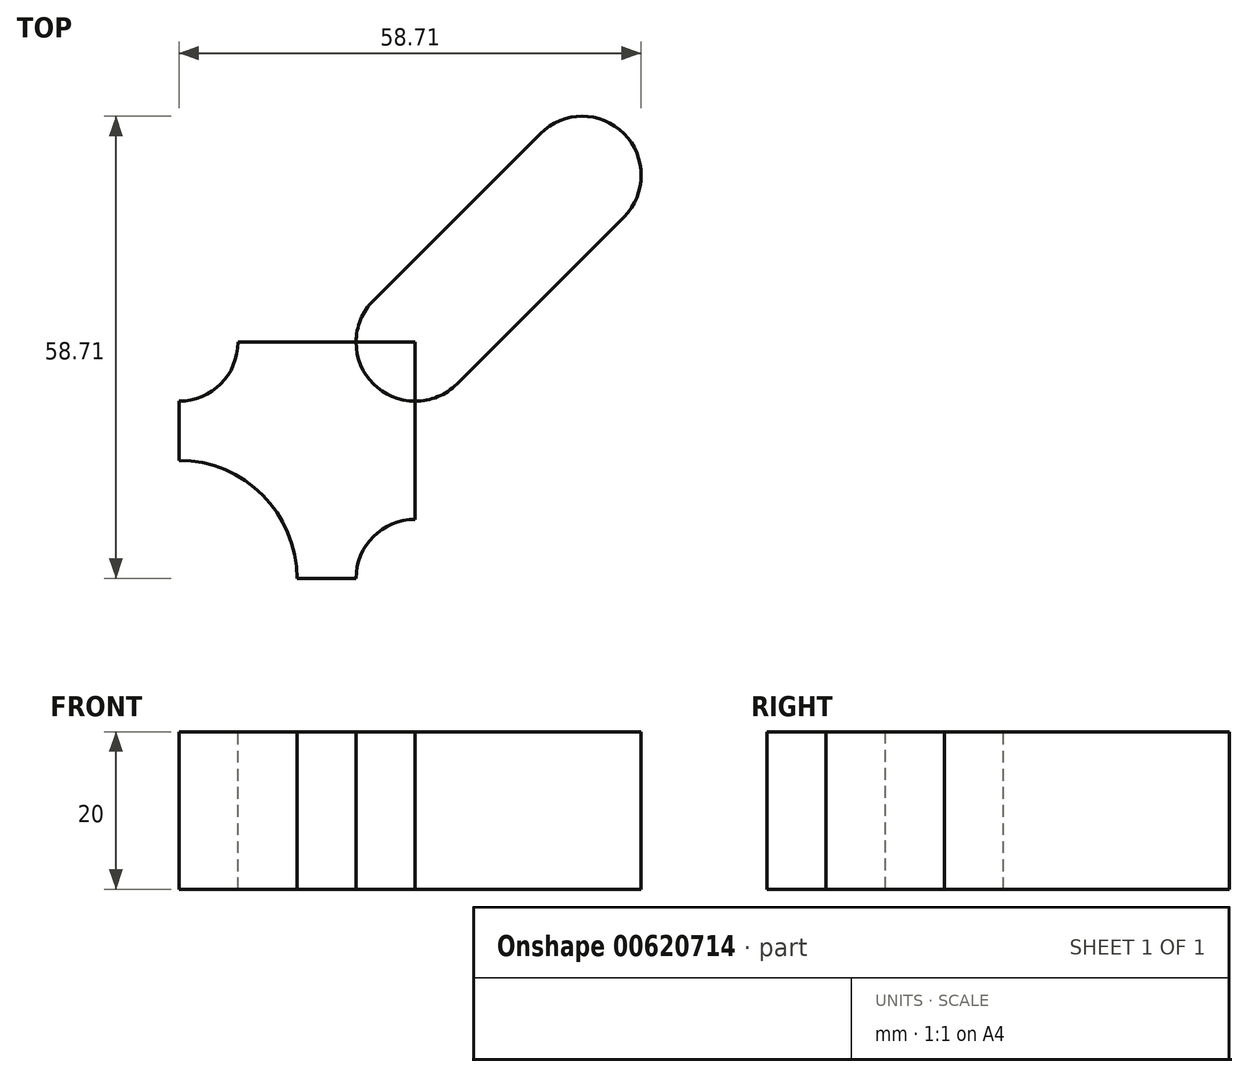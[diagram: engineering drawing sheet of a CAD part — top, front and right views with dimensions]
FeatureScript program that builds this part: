
annotation { "Feature Type Name" : "Feature", "Feature Type Description" : "" }
export const myFeature = defineFeature(function(context is Context, id is Id, definition is map)
    precondition{}
    {
        {
            var Q0;
            Q0=qCreatedBy(makeId("Top.planeOp"),FACE);
            var sketch = newSketch(context, id + "F0", { "sketchPlane" : qUnion([Q0])});
            skLineSegment(sketch, "E0.bottom", {"start": v(0, 0) * mm, "end": v(-45, 0) * mm});
            skLineSegment(sketch, "E0.left", {"start": v(0, 0) * mm, "end": v(0, 115) * mm});
            skArc(sketch, "E1", {"start": v(-45, 0) * mm, "mid": v(-55.6, 4.4) * mm, "end": v(-60, 15) * mm});
            skArc(sketch, "E2", {"start": v(-60, 15) * mm, "mid": v(-64.4, 25.6) * mm, "end": v(-75, 30) * mm});
            skArc(sketch, "E3", {"start": v(-75, 30) * mm, "mid": v(-85.6, 34.4) * mm, "end": v(-90, 45) * mm});
            skLineSegment(sketch, "E4", {"start": v(-45, 15) * mm, "end": v(-60, 15) * mm});
            skLineSegment(sketch, "E5", {"start": v(-60, 15) * mm, "end": v(-75, 15) * mm});
            skLineSegment(sketch, "E6", {"start": v(-75, 15) * mm, "end": v(-75, 30) * mm});
            skLineSegment(sketch, "E7", {"start": v(-75, 45) * mm, "end": v(-75, 30) * mm});
            skLineSegment(sketch, "E8", {"start": v(-75, 45) * mm, "end": v(-90, 45) * mm});
            skLineSegment(sketch, "E9", {"start": v(-90, 45) * mm, "end": v(-90, 65) * mm});
            skLineSegment(sketch, "E10", {"start": v(-95, 70) * mm, "end": v(-105, 70) * mm});
            skLineSegment(sketch, "E11", {"start": v(-105, 70) * mm, "end": v(-105, 110) * mm});
            skLineSegment(sketch, "E12", {"start": v(-105, 110) * mm, "end": v(-95, 110) * mm});
            skLineSegment(sketch, "E13", {"start": v(-95, 110) * mm, "end": v(-58.31, 119.83) * mm});
            skLineSegment(sketch, "E14", {"start": v(-55, 120.72) * mm, "end": v(-25, 120.72) * mm});
            skArc(sketch, "E15", {"start": v(-105, 70) * mm, "mid": v(-125, 90) * mm, "end": v(-105, 110) * mm});
            skCircle(sketch, "E16", {"center": v(-105, 90) * mm, "radius": 10 * mm});
            skArc(sketch, "E17", {"start": v(-54.7, 123.67) * mm, "mid": v(-38.51, 135.64) * mm, "end": v(-25, 120.72) * mm});
            skCircle(sketch, "E18", {"center": v(-40, 120.72) * mm, "radius": 7.5 * mm});
            skLineSegment(sketch, "E19", {"start": v(-25, 120.72) * mm, "end": v(-25, 118) * mm});
            skLineSegment(sketch, "E20", {"start": v(-22, 115) * mm, "end": v(0, 115) * mm});
            skLineSegment(sketch, "E21", {"start": v(-45, 0) * mm, "end": v(-45, 15) * mm});
            skPoint(sketch, "E22.visualSharp", {"position": v(-25, 115) * mm});
            skArc(sketch, "E22.filletArc", {"start": v(-25, 118) * mm, "mid": v(-24.12, 115.88) * mm, "end": v(-22, 115) * mm});
            skPoint(sketch, "E23.visualSharp", {"position": v(-55, 120.72) * mm});
            skArc(sketch, "E23.filletArc", {"start": v(-58.31, 119.83) * mm, "mid": v(-55.96, 121.24) * mm, "end": v(-54.7, 123.67) * mm});
            skPoint(sketch, "E24.visualSharp", {"position": v(-90, 70) * mm});
            skArc(sketch, "E24.filletArc", {"start": v(-90, 65) * mm, "mid": v(-91.46, 68.54) * mm, "end": v(-95, 70) * mm});
            skCircle(sketch, "E25", {"center": v(-45, 15) * mm, "radius": 7.5 * mm});
            skCircle(sketch, "E26", {"center": v(-75, 45) * mm, "radius": 7.5 * mm});
            skSolve(sketch);
        }
        {
            var Q0;
            Q0=makeQuery(id+"F0.imprint","IMPRINT",FACE,{"disambiguationData":[TD([[makeQuery(id+"F0.imprint","IMPRINT",EDGE,{"derivedFrom":sQuery(id+"F0.wireOp",EDGE,"E0.bottom")}),-1.0]])]});
            var Q1;
            {var subQ0=sQuery(id+"F0.wireOp",EDGE,"E15");Q1=makeQuery(id+"F0.imprint","IMPRINT",FACE,{"disambiguationData":[TD([[makeQuery(id+"F0.imprint","IMPRINT",EDGE,{"derivedFrom":subQ0}),-1.0]])]});}
            var Q2;
            Q2=makeQuery(id+"F0.imprint","IMPRINT",FACE,{"disambiguationData":[TD([[makeQuery(id+"F0.imprint","IMPRINT",EDGE,{"derivedFrom":sQuery(id+"F0.wireOp",EDGE,"E1")}),-1.0]])]});
            var Q3;
            Q3=makeQuery(id+"F0.imprint","IMPRINT",FACE,{"disambiguationData":[TD([[makeQuery(id+"F0.imprint","IMPRINT",EDGE,{"derivedFrom":sQuery(id+"F0.wireOp",EDGE,"E3")}),-1.0]])]});
            extrude(context, id + "F1", {"entities" : qUnion([Q0, Q1, Q2, Q3]), "depth" : 20 * mm, "offsetDistance" : 25 * mm});
        }
        {
            var Q0;
            Q0=makeQuery(id+"F1.opExtrude","SWEPT_EDGE",EDGE,{"disambiguationData":[OSD([sQuery(id+"F0.wireOp",EDGE,"E0.left"),sQuery(id+"F0.wireOp",EDGE,"E20")])]});
            var Q1;
            Q1=makeQuery(id+"F1.opExtrude","SWEPT_EDGE",EDGE,{"disambiguationData":[OSD([sQuery(id+"F0.wireOp",EDGE,"E0.bottom"),sQuery(id+"F0.wireOp",EDGE,"E0.left")])]});
            chamfer(context, id + "F2", {"entities" : qUnion([Q0, Q1]), "width" : 5 * mm, "tangentPropagation" : true});
        }
        {
            var Q0;
            Q0=makeQuery(id+"F1.opExtrude","CAP_FACE",FACE,{"disambiguationData":[OSD([sQuery(id+"F0.wireOp",EDGE,"E0.bottom"),sQuery(id+"F0.wireOp",EDGE,"E0.left"),sQuery(id+"F0.wireOp",EDGE,"E1"),sQuery(id+"F0.wireOp",EDGE,"E2"),sQuery(id+"F0.wireOp",EDGE,"E3"),sQuery(id+"F0.wireOp",EDGE,"E9"),sQuery(id+"F0.wireOp",EDGE,"E10"),sQuery(id+"F0.wireOp",EDGE,"E12"),sQuery(id+"F0.wireOp",EDGE,"E13"),sQuery(id+"F0.wireOp",EDGE,"E15"),sQuery(id+"F0.wireOp",EDGE,"E16"),sQuery(id+"F0.wireOp",EDGE,"E17"),sQuery(id+"F0.wireOp",EDGE,"E18"),sQuery(id+"F0.wireOp",EDGE,"E19"),sQuery(id+"F0.wireOp",EDGE,"E20"),sQuery(id+"F0.wireOp",EDGE,"E22.filletArc"),sQuery(id+"F0.wireOp",EDGE,"E23.filletArc"),sQuery(id+"F0.wireOp",EDGE,"E24.filletArc"),sQuery(id+"F0.wireOp",EDGE,"E25"),sQuery(id+"F0.wireOp",EDGE,"E26")])],"isStart":false});
            var sketch = newSketch(context, id + "F3", { "sketchPlane" : qUnion([Q0])});
            skLineSegment(sketch, "E27", {"start": v(-45, 15) * mm, "end": v(-45, 45) * mm});
            skLineSegment(sketch, "E28", {"start": v(-45, 45) * mm, "end": v(-75, 45) * mm});
            skLineSegment(sketch, "E29", {"start": v(-45, 45) * mm, "end": v(-23.79, 66.21) * mm});
            skArc(sketch, "E30.0.startCap", {"start": v(-39.7, 39.7) * mm, "mid": v(-50.3, 39.7) * mm, "end": v(-50.3, 50.3) * mm});
            skArc(sketch, "E30.0.endCap", {"start": v(-29.1, 71.52) * mm, "mid": v(-18.48, 71.52) * mm, "end": v(-18.48, 60.9) * mm});
            skLineSegment(sketch, "E30.0.left", {"start": v(-50.3, 50.3) * mm, "end": v(-29.1, 71.52) * mm});
            skLineSegment(sketch, "E30.0.right", {"start": v(-39.7, 39.7) * mm, "end": v(-18.48, 60.9) * mm});
            skSolve(sketch);
        }
        {
            var Q0;
            Q0=makeQuery(id+"F3.imprint","IMPRINT",FACE,{"disambiguationData":[TD([[makeQuery(id+"F3.imprint","IMPRINT",EDGE,{"derivedFrom":sQuery(id+"F3.wireOp",EDGE,"E30.0.endCap")}),-1.0]])]});
            var Q1;
            {var subQ0=sQuery(id+"F3.wireOp",EDGE,"E28");var subQ1=sQuery(id+"F3.wireOp",EDGE,"E27");var subQ2=makeQuery(id+"F3.imprint","INTERSECT",VERTEX,{"derivedFrom":[subQ1,subQ0]});Q1=makeQuery(id+"F3.imprint","IMPRINT",FACE,{"disambiguationData":[TD([[makeQuery(id+"F3.imprint","IMPRINT",EDGE,{"disambiguationData":[TD([[subQ2,1.0]])],"derivedFrom":subQ1}),1.0]])]});}
            extrude(context, id + "F4", {"entities" : qUnion([Q0, Q1]), "operationType" : NewBodyOperationType.REMOVE, "oppositeDirection" : true, "depth" : 25 * mm, "offsetDistance" : 25 * mm});
        }
    });
